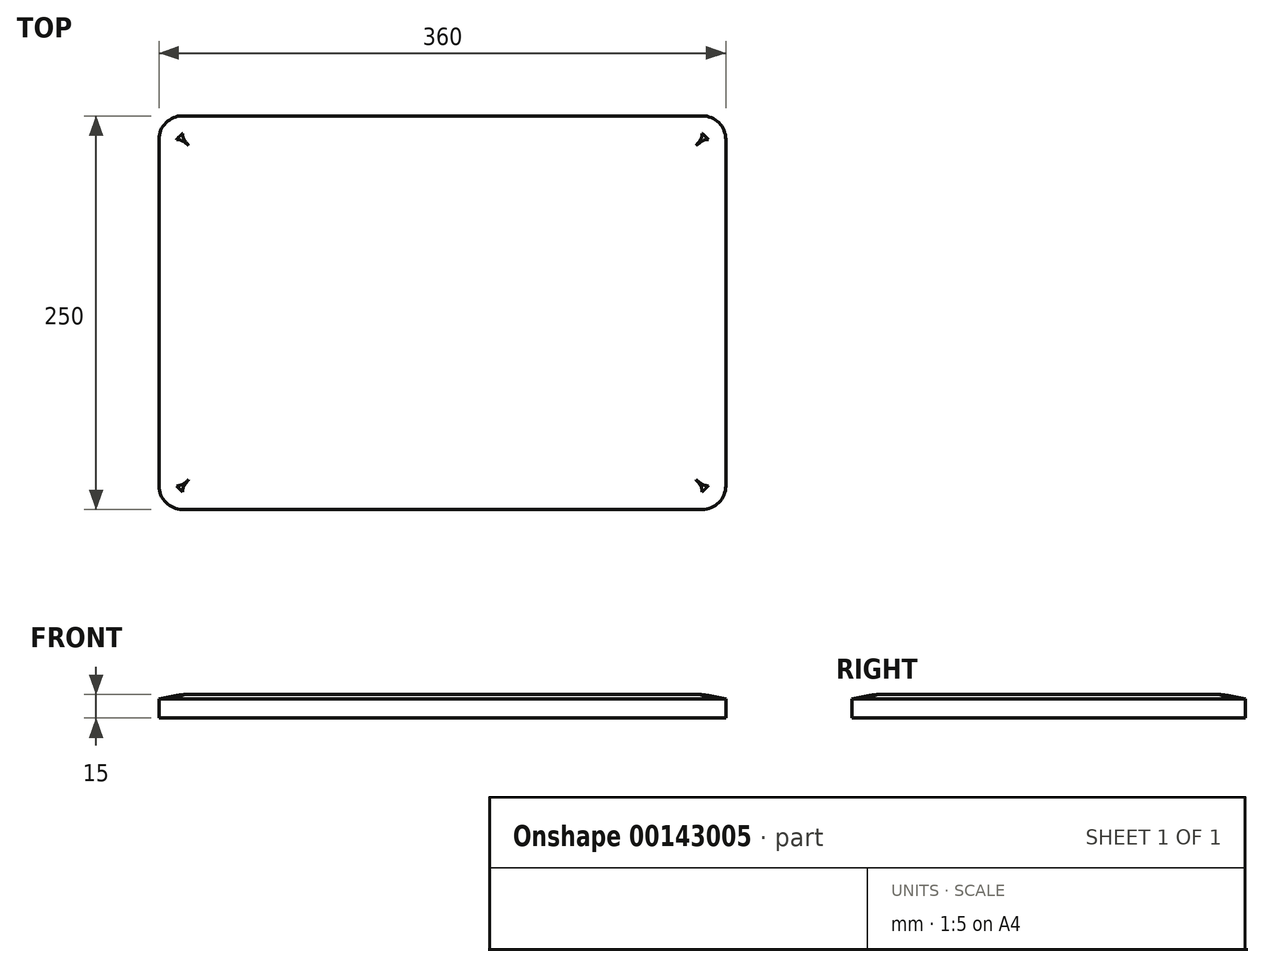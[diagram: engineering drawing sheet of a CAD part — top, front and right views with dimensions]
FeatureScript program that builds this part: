
annotation { "Feature Type Name" : "Feature", "Feature Type Description" : "" }
export const myFeature = defineFeature(function(context is Context, id is Id, definition is map)
    precondition{}
    {
        {
            var Q0;
            Q0=qCreatedBy(makeId("Top.planeOp"),FACE);
            var sketch = newSketch(context, id + "F0", { "sketchPlane" : qUnion([Q0])});
            skLineSegment(sketch, "E0.bottom", {"start": v(15, 0) * mm, "end": v(345, 0) * mm});
            skLineSegment(sketch, "E0.top", {"start": v(15, 250) * mm, "end": v(345, 250) * mm});
            skLineSegment(sketch, "E0.left", {"start": v(0, 15) * mm, "end": v(0, 235) * mm});
            skLineSegment(sketch, "E0.right", {"start": v(360, 15) * mm, "end": v(360, 235) * mm});
            skPoint(sketch, "E1.visualSharp", {"position": v(0, 250) * mm});
            skArc(sketch, "E1.filletArc", {"start": v(15, 250) * mm, "mid": v(4.4, 245.6) * mm, "end": v(0, 235) * mm});
            skPoint(sketch, "E2.visualSharp", {"position": v(0, 0) * mm});
            skArc(sketch, "E2.filletArc", {"start": v(0, 15) * mm, "mid": v(4.4, 4.4) * mm, "end": v(15, 0) * mm});
            skPoint(sketch, "E3.visualSharp", {"position": v(360, 0) * mm});
            skArc(sketch, "E3.filletArc", {"start": v(345, 0) * mm, "mid": v(355.6, 4.4) * mm, "end": v(360, 15) * mm});
            skPoint(sketch, "E4.visualSharp", {"position": v(360, 250) * mm});
            skArc(sketch, "E4.filletArc", {"start": v(360, 235) * mm, "mid": v(355.6, 245.6) * mm, "end": v(345, 250) * mm});
            skSolve(sketch);
        }
        {
            var Q0;
            Q0 = qSketchRegion(id + "F0", true);
            extrude(context, id + "F1", {"entities" : qUnion([Q0]), "depth" : 15 * mm});
        }
        {
            var Q0;
            Q0=makeQuery(id+"F1.opExtrude","CAP_FACE",FACE,{"disambiguationData":[OSD([sQuery(id+"F0.wireOp",EDGE,"E0.bottom"),sQuery(id+"F0.wireOp",EDGE,"E0.top"),sQuery(id+"F0.wireOp",EDGE,"E0.left"),sQuery(id+"F0.wireOp",EDGE,"E0.right"),sQuery(id+"F0.wireOp",EDGE,"E1.filletArc"),sQuery(id+"F0.wireOp",EDGE,"E2.filletArc"),sQuery(id+"F0.wireOp",EDGE,"E3.filletArc"),sQuery(id+"F0.wireOp",EDGE,"E4.filletArc")])],"isStart":false});
            chamfer(context, id + "F2", {"entities" : qUnion([Q0]), "chamferType" : ChamferType.TWO_OFFSETS, "width1" : 15 * mm, "oppositeDirection" : false, "width2" : 3 * mm, "tangentPropagation" : true});
        }
        {
            var Q0;
            Q0=makeQuery(id+"F1.opExtrude","CAP_FACE",FACE,{"disambiguationData":[OSD([sQuery(id+"F0.wireOp",EDGE,"E0.bottom"),sQuery(id+"F0.wireOp",EDGE,"E0.top"),sQuery(id+"F0.wireOp",EDGE,"E0.left"),sQuery(id+"F0.wireOp",EDGE,"E0.right"),sQuery(id+"F0.wireOp",EDGE,"E1.filletArc"),sQuery(id+"F0.wireOp",EDGE,"E2.filletArc"),sQuery(id+"F0.wireOp",EDGE,"E3.filletArc"),sQuery(id+"F0.wireOp",EDGE,"E4.filletArc")])],"isStart":false});
            fillet(context, id + "F3", {"entities" : qUnion([Q0]), "radius" : 40 * mm, "allowEdgeOverflow" : false});
        }
    });
